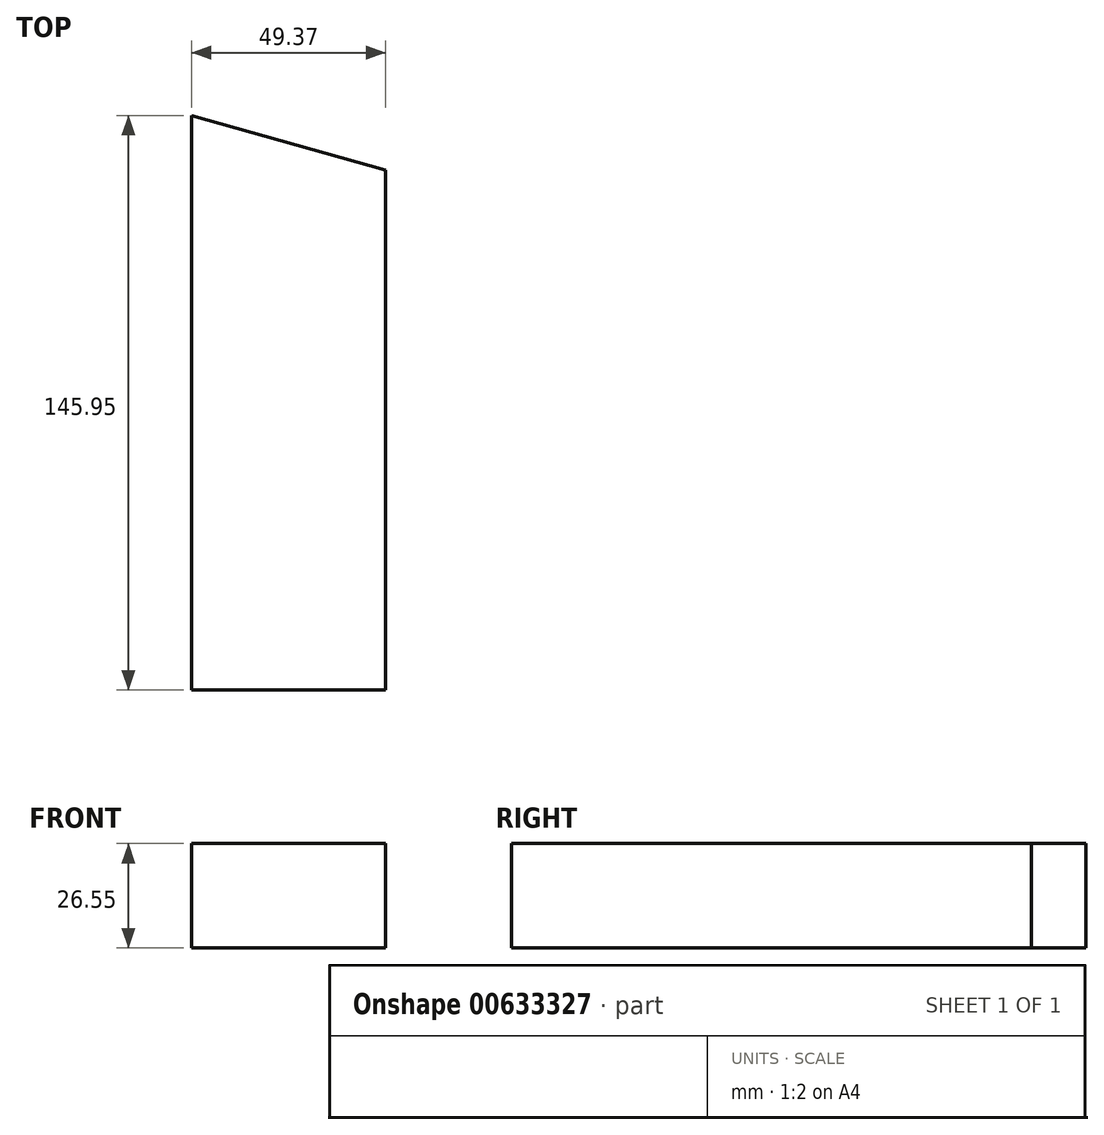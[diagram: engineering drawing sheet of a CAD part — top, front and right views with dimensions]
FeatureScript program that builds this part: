
annotation { "Feature Type Name" : "Feature", "Feature Type Description" : "" }
export const myFeature = defineFeature(function(context is Context, id is Id, definition is map)
    precondition{}
    {
        {
            var Q0;
            Q0=qCreatedBy(makeId("Top.planeOp"),FACE);
            var sketch = newSketch(context, id + "F0", { "sketchPlane" : qUnion([Q0])});
            skLineSegment(sketch, "E0", {"start": v(0, 70.43) * mm, "end": v(49.37, 56.57) * mm});
            skLineSegment(sketch, "E1", {"start": v(49.37, 56.57) * mm, "end": v(49.37, -75.52) * mm});
            skLineSegment(sketch, "E2", {"start": v(49.37, -75.52) * mm, "end": v(0, -75.52) * mm});
            skLineSegment(sketch, "E3", {"start": v(0, -75.52) * mm, "end": v(0, 70.43) * mm});
            skSolve(sketch);
        }
        {
            var Q0;
            Q0 = qSketchRegion(id + "F0", true);
            extrude(context, id + "F1", {"entities" : qUnion([Q0]), "depth" : 26.55 * mm, "offsetDistance" : 25.4 * mm});
        }
    });
